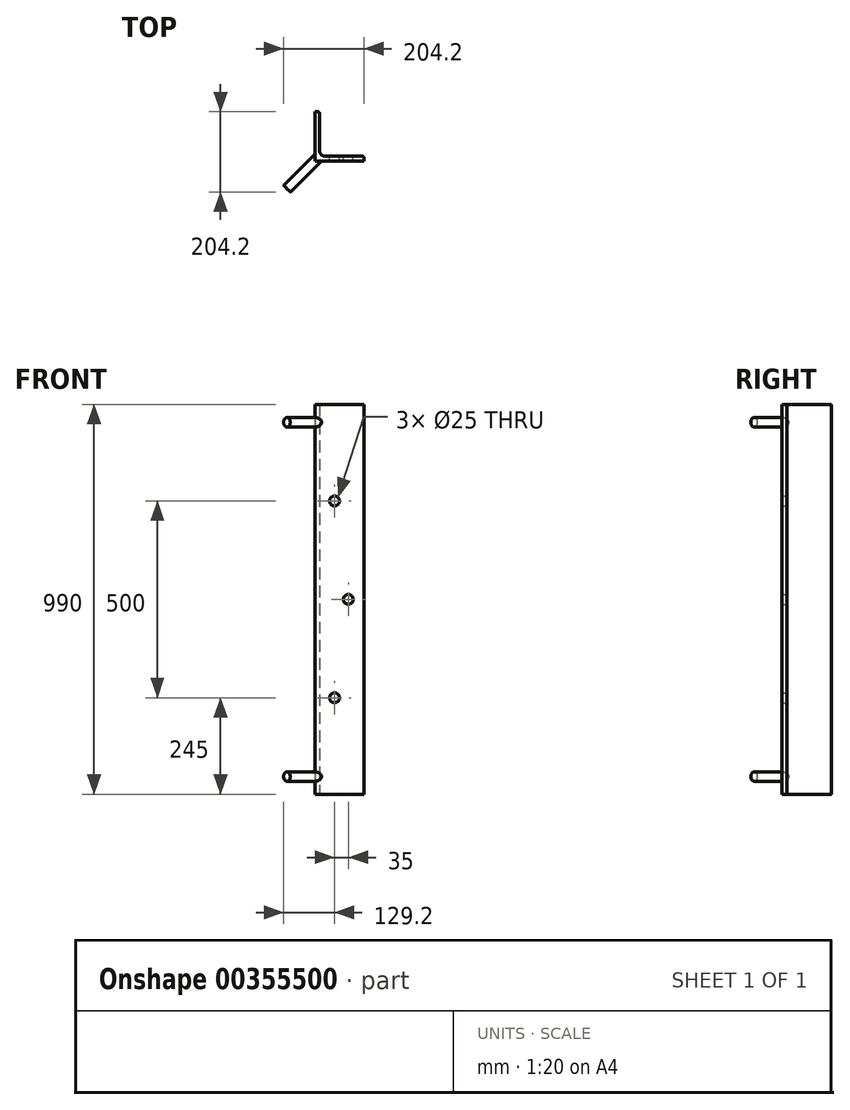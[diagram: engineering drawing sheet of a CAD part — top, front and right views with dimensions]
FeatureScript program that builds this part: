
annotation { "Feature Type Name" : "Feature", "Feature Type Description" : "" }
export const myFeature = defineFeature(function(context is Context, id is Id, definition is map)
    precondition{}
    {
        {
            var Q0;
            Q0=qCreatedBy(makeId("Top.planeOp"),FACE);
            var sketch = newSketch(context, id + "F0", { "sketchPlane" : qUnion([Q0])});
            skLineSegment(sketch, "E0", {"start": v(0, 0) * mm, "end": v(125, 0) * mm});
            skLineSegment(sketch, "E1", {"start": v(125, 0) * mm, "end": v(125, 12) * mm});
            skLineSegment(sketch, "E2", {"start": v(0, 125) * mm, "end": v(12, 125) * mm});
            skLineSegment(sketch, "E3", {"start": v(0, 0) * mm, "end": v(0, 125) * mm});
            skLineSegment(sketch, "E4", {"start": v(12, 125) * mm, "end": v(12, 12) * mm});
            skLineSegment(sketch, "E5", {"start": v(12, 12) * mm, "end": v(125, 12) * mm});
            skSolve(sketch);
        }
        {
            var Q0;
            Q0=makeQuery(id+"F0.imprint","IMPRINT",FACE,{"disambiguationData":[TD([[makeQuery(id+"F0.imprint","IMPRINT",EDGE,{"derivedFrom":sQuery(id+"F0.wireOp",EDGE,"E0")}),1.0]])]});
            extrude(context, id + "F1", {"entities" : qUnion([Q0]), "endBound" : BoundingType.SYMMETRIC, "depth" : 990 * mm});
        }
        {
            var Q0;
            Q0=makeQuery(id+"F1.opExtrude","SWEPT_EDGE",EDGE,{"disambiguationData":[OSD([sQuery(id+"F0.wireOp",EDGE,"E4"),sQuery(id+"F0.wireOp",EDGE,"E5")])]});
            fillet(context, id + "F2", {"entities" : qUnion([Q0]), "radius" : 14 * mm, "tangentPropagation" : true, "allowEdgeOverflow" : false});
        }
        {
            var Q0;
            Q0=makeQuery(id+"F1.opExtrude","SWEPT_EDGE",EDGE,{"disambiguationData":[OSD([sQuery(id+"F0.wireOp",EDGE,"E2"),sQuery(id+"F0.wireOp",EDGE,"E4")])]});
            var Q1;
            Q1=makeQuery(id+"F1.opExtrude","SWEPT_EDGE",EDGE,{"disambiguationData":[OSD([sQuery(id+"F0.wireOp",EDGE,"E1"),sQuery(id+"F0.wireOp",EDGE,"E5")])]});
            fillet(context, id + "F3", {"entities" : qUnion([Q0, Q1]), "radius" : 4.6 * mm, "tangentPropagation" : true, "allowEdgeOverflow" : false});
        }
        {
            var Q0;
            Q0=makeQuery(id+"F1.opExtrude","SWEPT_FACE",FACE,{"disambiguationData":[OSD([sQuery(id+"F0.wireOp",EDGE,"E5")])]});
            var sketch = newSketch(context, id + "F4", { "sketchPlane" : qUnion([Q0])});
            skCircle(sketch, "E6", {"center": v(-85, 0) * mm, "radius": 12.5 * mm});
            skCircle(sketch, "E7", {"center": v(-50, -250) * mm, "radius": 12.5 * mm});
            skCircle(sketch, "E8.MirrorC", {"center": v(-50, 250) * mm, "radius": 12.5 * mm});
            skSolve(sketch);
        }
        {
            var Q0;
            Q0=qCreatedBy(makeId("Front.planeOp"),FACE);
            var Q1;
            Q1=makeQuery(id+"F1.opExtrude","SWEPT_EDGE",EDGE,{"disambiguationData":[OSD([sQuery(id+"F0.wireOp",EDGE,"E0"),sQuery(id+"F0.wireOp",EDGE,"E3")])]});
            cPlane(context, id + "F5", {"entities" : qUnion([Q0, Q1]), "cplaneType" : CPlaneType.LINE_ANGLE, "offset" : 25 * mm, "angle" : 45 * degree, "width" : 150 * mm, "height" : 150 * mm});
        }
        {
            var Q0;
            Q0=qCreatedBy(id+"F5.planeOp",FACE);
            var sketch = newSketch(context, id + "F6", { "sketchPlane" : qUnion([Q0])});
            skCircle(sketch, "E9", {"center": v(0, 450) * mm, "radius": 12 * mm});
            skCircle(sketch, "E10.MirrorC", {"center": v(0, -450) * mm, "radius": 12 * mm});
            skSolve(sketch);
        }
        {
            var Q0;
            Q0 = qSketchRegion(id + "F6", true);
            extrude(context, id + "F7", {"entities" : qUnion([Q0]), "operationType" : NewBodyOperationType.ADD, "depth" : 20 * mm, "hasSecondDirection" : true, "secondDirectionOppositeDirection" : true, "secondDirectionDepth" : 100 * mm});
        }
        {
            var Q0;
            Q0 = qSketchRegion(id + "F4", true);
            extrude(context, id + "F8", {"entities" : qUnion([Q0]), "operationType" : NewBodyOperationType.REMOVE, "endBound" : BoundingType.THROUGH_ALL, "oppositeDirection" : true, "depth" : 25 * mm});
        }
    });
